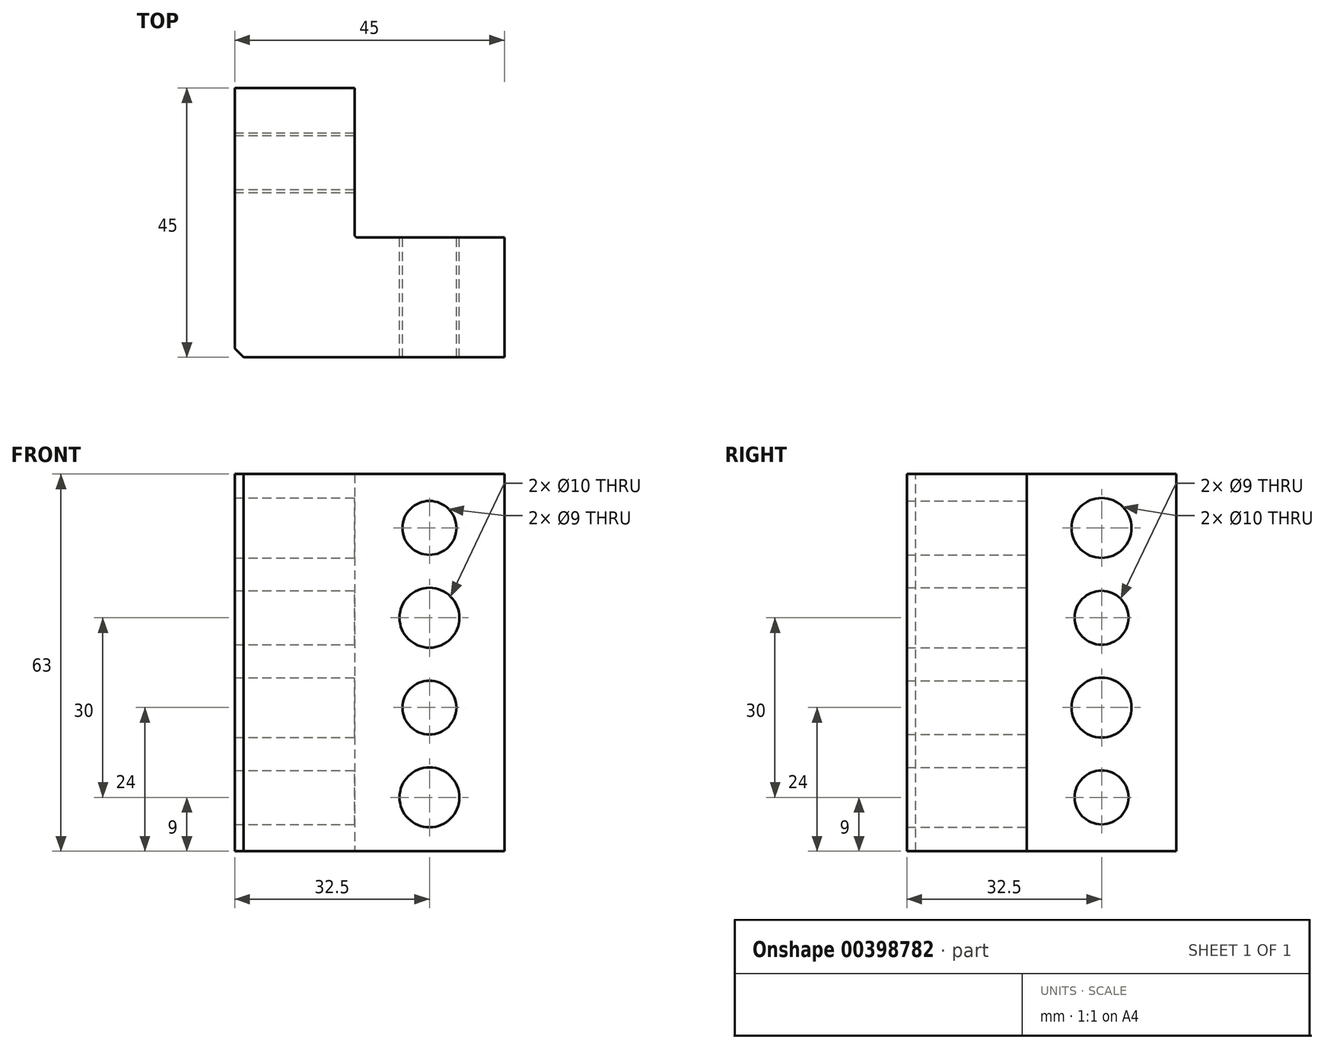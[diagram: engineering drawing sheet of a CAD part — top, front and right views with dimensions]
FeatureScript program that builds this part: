
annotation { "Feature Type Name" : "Feature", "Feature Type Description" : "" }
export const myFeature = defineFeature(function(context is Context, id is Id, definition is map)
    precondition{}
    {
        {
            var Q0;
            Q0=qCreatedBy(makeId("Top.planeOp"),FACE);
            var sketch = newSketch(context, id + "F0", { "sketchPlane" : qUnion([Q0])});
            skLineSegment(sketch, "E0", {"start": v(0, 0) * mm, "end": v(-45, 0) * mm});
            skLineSegment(sketch, "E1", {"start": v(-45, 0) * mm, "end": v(-45, 45) * mm});
            skLineSegment(sketch, "E2", {"start": v(-45, 45) * mm, "end": v(-25, 45) * mm});
            skLineSegment(sketch, "E3", {"start": v(-25, 45) * mm, "end": v(-25, 20) * mm});
            skLineSegment(sketch, "E4", {"start": v(-25, 20) * mm, "end": v(0, 20) * mm});
            skLineSegment(sketch, "E5", {"start": v(0, 20) * mm, "end": v(0, 0) * mm});
            skSolve(sketch);
        }
        {
            var Q0;
            Q0 = qSketchRegion(id + "F0", true);
            extrude(context, id + "F1", {"entities" : qUnion([Q0]), "depth" : 63 * mm});
        }
        {
            var Q0;
            Q0=makeQuery(id+"F1.opExtrude","SWEPT_FACE",FACE,{"disambiguationData":[OSD([sQuery(id+"F0.wireOp",EDGE,"E3")])]});
            var sketch = newSketch(context, id + "F2", { "sketchPlane" : qUnion([Q0])});
            skLineSegment(sketch, "E6", {"start": v(32.5, 0) * mm, "end": v(32.5, 9) * mm, "construction": true});
            skLineSegment(sketch, "E7", {"start": v(32.5, 9) * mm, "end": v(32.5, 24) * mm, "construction": true});
            skLineSegment(sketch, "E8", {"start": v(32.5, 24) * mm, "end": v(32.5, 39) * mm, "construction": true});
            skCircle(sketch, "E9", {"center": v(32.5, 9) * mm, "radius": 4.5 * mm});
            skCircle(sketch, "E10", {"center": v(32.5, 24) * mm, "radius": 5 * mm});
            skCircle(sketch, "E11", {"center": v(32.5, 39) * mm, "radius": 4.5 * mm});
            skLineSegment(sketch, "E12", {"start": v(32.5, 39) * mm, "end": v(32.5, 54) * mm, "construction": true});
            skLineSegment(sketch, "E13", {"start": v(32.5, 54) * mm, "end": v(32.5, 63) * mm, "construction": true});
            skCircle(sketch, "E14", {"center": v(32.5, 54) * mm, "radius": 5 * mm});
            skSolve(sketch);
        }
        {
            var Q0;
            Q0=makeQuery(id+"F2.imprint","IMPRINT",FACE,{"disambiguationData":[TD([[makeQuery(id+"F2.imprint","IMPRINT",EDGE,{"derivedFrom":sQuery(id+"F2.wireOp",EDGE,"E11")}),1.0]])]});
            var Q1;
            Q1=makeQuery(id+"F2.imprint","IMPRINT",FACE,{"disambiguationData":[TD([[makeQuery(id+"F2.imprint","IMPRINT",EDGE,{"derivedFrom":sQuery(id+"F2.wireOp",EDGE,"E10")}),1.0]])]});
            var Q2;
            Q2=makeQuery(id+"F2.imprint","IMPRINT",FACE,{"disambiguationData":[TD([[makeQuery(id+"F2.imprint","IMPRINT",EDGE,{"derivedFrom":sQuery(id+"F2.wireOp",EDGE,"E9")}),1.0]])]});
            var Q3;
            Q3=makeQuery(id+"F2.imprint","IMPRINT",FACE,{"disambiguationData":[TD([[makeQuery(id+"F2.imprint","IMPRINT",EDGE,{"derivedFrom":sQuery(id+"F2.wireOp",EDGE,"E14")}),1.0]])]});
            extrude(context, id + "F3", {"entities" : qUnion([Q0, Q1, Q2, Q3]), "operationType" : NewBodyOperationType.REMOVE, "oppositeDirection" : true, "depth" : 25 * mm});
        }
        {
            var Q0;
            Q0=makeQuery(id+"F1.opExtrude","SWEPT_FACE",FACE,{"disambiguationData":[OSD([sQuery(id+"F0.wireOp",EDGE,"E4")])]});
            var sketch = newSketch(context, id + "F4", { "sketchPlane" : qUnion([Q0])});
            skLineSegment(sketch, "E15", {"start": v(12.5, 63) * mm, "end": v(12.5, 54) * mm, "construction": true});
            skPoint(sketch, "E15.endSnap0", {"position": v(12.5, 63) * mm});
            skLineSegment(sketch, "E16", {"start": v(12.5, 54) * mm, "end": v(12.5, 39) * mm, "construction": true});
            skLineSegment(sketch, "E17", {"start": v(12.5, 39) * mm, "end": v(12.5, 24) * mm, "construction": true});
            skPoint(sketch, "E17.endSnap0", {"position": v(12.5, 46.5) * mm});
            skCircle(sketch, "E18", {"center": v(12.5, 54) * mm, "radius": 4.5 * mm});
            skCircle(sketch, "E19", {"center": v(12.5, 39) * mm, "radius": 5 * mm});
            skCircle(sketch, "E20", {"center": v(12.5, 24) * mm, "radius": 4.5 * mm});
            skLineSegment(sketch, "E21", {"start": v(12.5, 24) * mm, "end": v(12.5, 9) * mm, "construction": true});
            skLineSegment(sketch, "E22", {"start": v(12.5, 9) * mm, "end": v(12.5, 0) * mm, "construction": true});
            skCircle(sketch, "E23", {"center": v(12.5, 9) * mm, "radius": 5 * mm});
            skSolve(sketch);
        }
        {
            var Q0;
            Q0 = qSketchRegion(id + "F4", true);
            extrude(context, id + "F5", {"entities" : qUnion([Q0]), "operationType" : NewBodyOperationType.REMOVE, "oppositeDirection" : true, "depth" : 25 * mm});
        }
        {
            var Q0;
            Q0=makeQuery(id+"F1.opExtrude","SWEPT_EDGE",EDGE,{"disambiguationData":[OSD([sQuery(id+"F0.wireOp",EDGE,"E3"),sQuery(id+"F0.wireOp",EDGE,"E4")])]});
            fillet(context, id + "F6", {"entities" : qUnion([Q0]), "radius" : .5 * mm, "tangentPropagation" : true, "allowEdgeOverflow" : false});
        }
        {
            var Q0;
            Q0=makeQuery(id+"F1.opExtrude","SWEPT_EDGE",EDGE,{"disambiguationData":[OSD([sQuery(id+"F0.wireOp",EDGE,"E0"),sQuery(id+"F0.wireOp",EDGE,"E1")])]});
            chamfer(context, id + "F7", {"entities" : qUnion([Q0]), "width" : 1.5 * mm, "tangentPropagation" : true});
        }
    });
